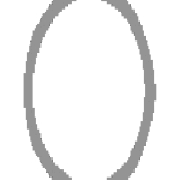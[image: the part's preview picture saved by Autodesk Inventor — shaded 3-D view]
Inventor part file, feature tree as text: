
AUTODESK INVENTOR PART (.ipt)
format: ipt  version: 2021 (Build 250183000, 183)  size: 113,152 bytes
history: native  units: in
note: dims shown in document units (in); Inventor stores cm internally (conversion verified against a paired STEP export)
features: other x4, sketch x3, plane x1
ambient origin geometry x8: Origin, YZ Plane, XZ Plane, XY Plane, X Axis, Y Axis, Z Axis, Center Point
bodies: Solid1 (feature_tree), Body (feature_tree)
feature tree (8):
  other  "Driven Length"
  other  "Frame Generator"
  other  "Start Plane"
  other  "End Plane"
  sketch  "Sketch"  dims[d2=11.5in d4=-0.0in d5=11.5in d6=0.12in d7=0.0in d8=90.0deg d9=11.5in]
  sketch  "Sketch2"  dims[d0=1.0in]
  plane  "Work Plane3"
  sketch  "Sketch3"  dims[d1=0.065in]
